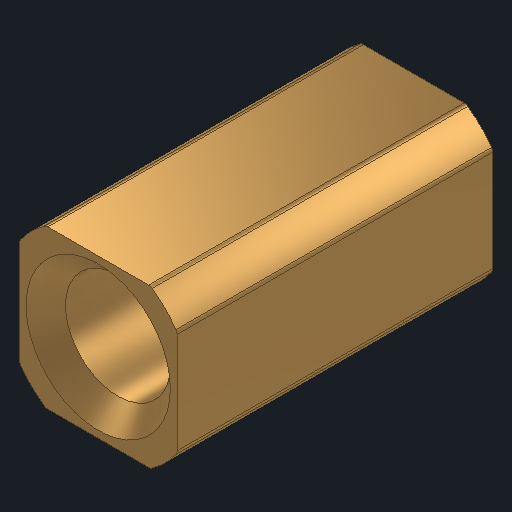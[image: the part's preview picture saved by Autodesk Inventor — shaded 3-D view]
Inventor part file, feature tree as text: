
AUTODESK INVENTOR PART (.ipt)
format: ipt  version: 2024 (Build 280153000, 153)  size: 164,864 bytes
history: native  units: in
note: dims shown in document units (in); Inventor stores cm internally (conversion verified against a paired STEP export)
features: other x3, sketch x2
ambient origin geometry x8: Origin, YZ Plane, XZ Plane, XY Plane, X Axis, Y Axis, Z Axis, Center Point
bodies: Solid1 (feature_tree)
feature tree (5):
  other  "HS Shaft Adapter Circle.ipt"
  other  "Solid1::HS Shaft Adapter Circle.ipt"
  other  "TaggingFeature1"
  sketch  "Sketch1"  dims[d0=0.3937in]
  sketch  "Sketch2"
